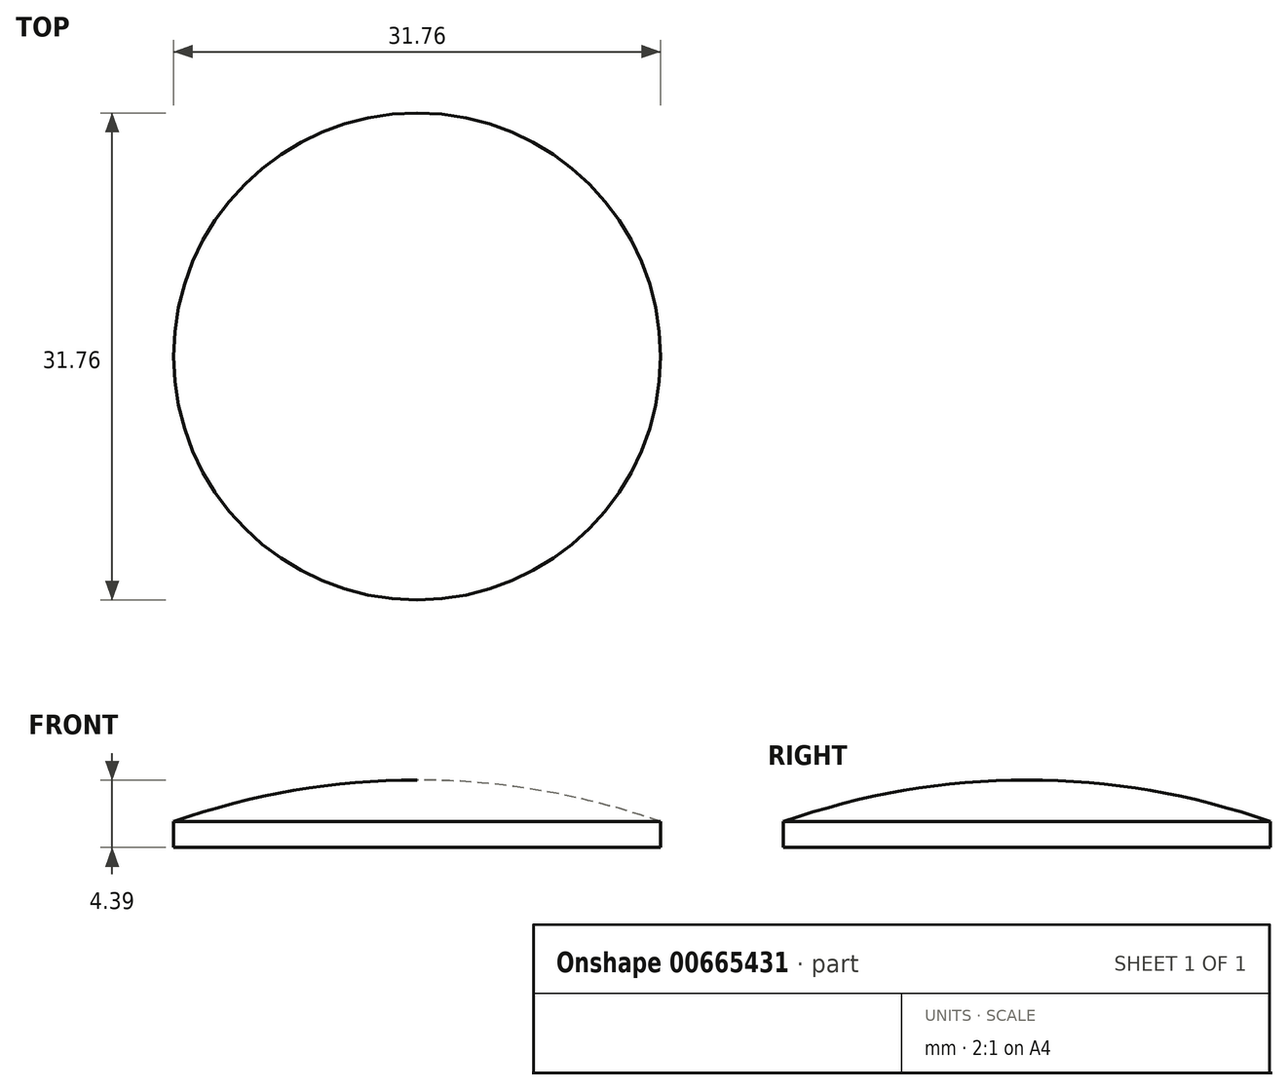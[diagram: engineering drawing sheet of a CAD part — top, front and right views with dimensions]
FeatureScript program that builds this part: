
annotation { "Feature Type Name" : "Feature", "Feature Type Description" : "" }
export const myFeature = defineFeature(function(context is Context, id is Id, definition is map)
    precondition{}
    {
        {
            var Q0;
            Q0=qCreatedBy(makeId("Front.planeOp"),FACE);
            var sketch = newSketch(context, id + "F0", { "sketchPlane" : qUnion([Q0])});
            skLineSegment(sketch, "E0.bottom", {"start": v(0, -1.4) * mm, "end": v(-15.88, -1.4) * mm});
            skLineSegment(sketch, "E0.right", {"start": v(-15.88, -1.4) * mm, "end": v(-15.88, 0.27) * mm});
            skPoint(sketch, "E0.middle", {"position": v(0, 0) * mm});
            skArc(sketch, "E1", {"start": v(0, 2.98) * mm, "mid": v(-8.05, 2.3) * mm, "end": v(-15.88, 0.27) * mm});
            skLineSegment(sketch, "E2", {"start": v(0, 2.98) * mm, "end": v(0, -1.4) * mm});
            skSolve(sketch);
        }
        {
            var Q0;
            Q0=makeQuery(id+"F0.imprint","IMPRINT",FACE,{"disambiguationData":[TD([[makeQuery(id+"F0.imprint","IMPRINT",EDGE,{"derivedFrom":sQuery(id+"F0.wireOp",EDGE,"E0.bottom")}),-1.0]])]});
            var Q1;
            Q1=sQuery(id+"F0.wireOp",EDGE,"E2");
            revolve(context, id + "F1", {"surfaceOperationType" : NewSurfaceOperationType.NEW, "entities" : qUnion([Q0]), "axis" : qUnion([Q1]), "revolveType" : RevolveType.FULL});
        }
    });
